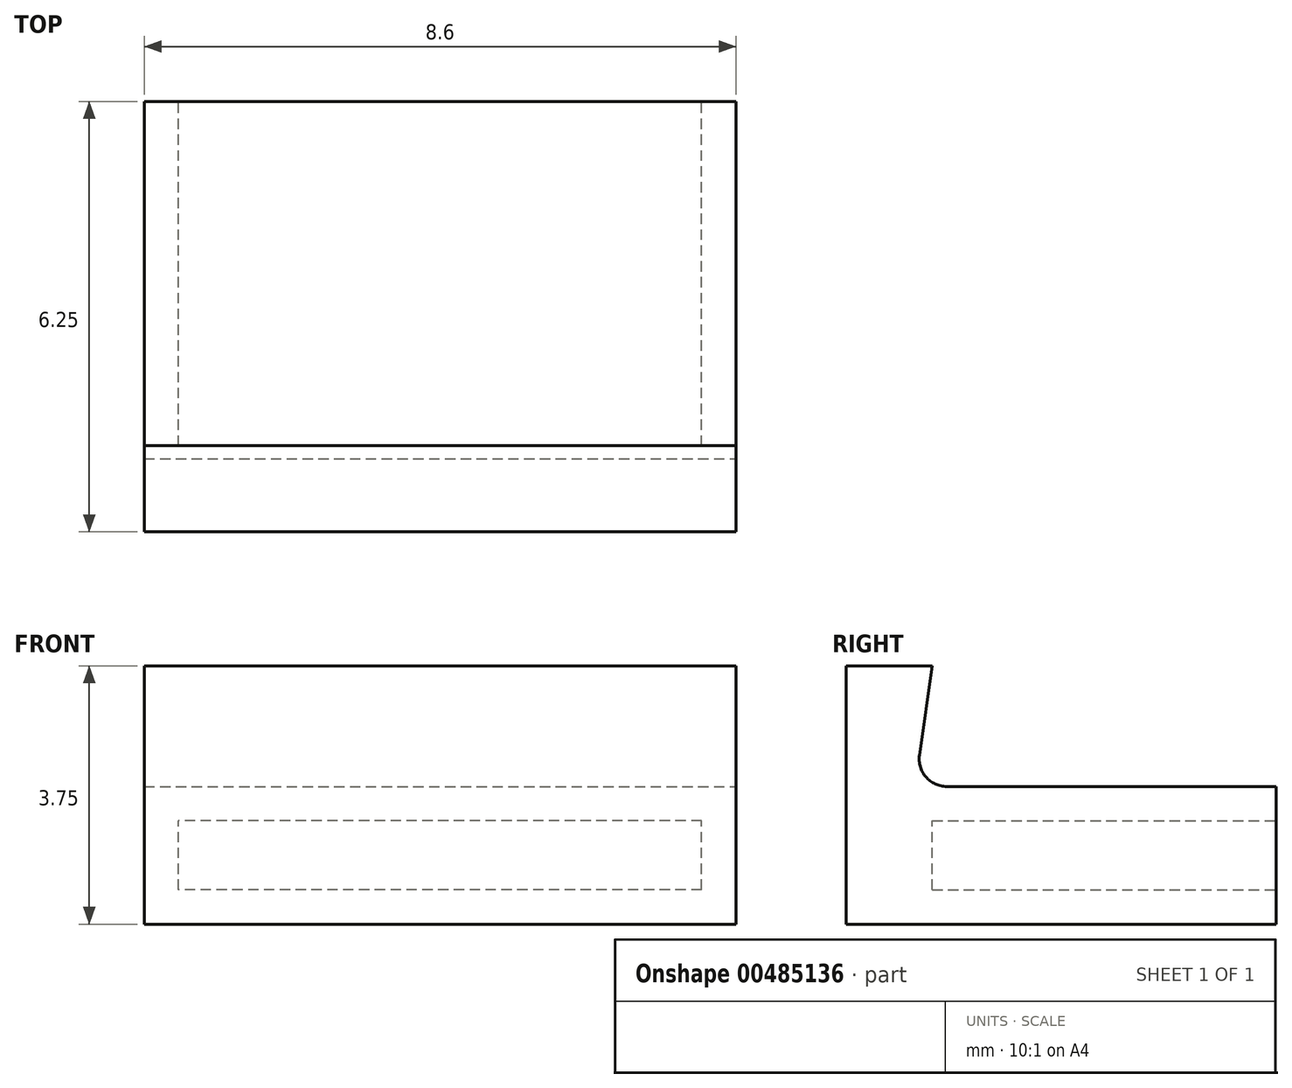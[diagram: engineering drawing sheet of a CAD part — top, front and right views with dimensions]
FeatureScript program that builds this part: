
annotation { "Feature Type Name" : "Feature", "Feature Type Description" : "" }
export const myFeature = defineFeature(function(context is Context, id is Id, definition is map)
    precondition{}
    {
        {
            var Q0;
            Q0=qCreatedBy(makeId("Front.planeOp"),FACE);
            var sketch = newSketch(context, id + "F0", { "sketchPlane" : qUnion([Q0])});
            skLineSegment(sketch, "E0.bottom", {"start": v(3.8, -0.5) * mm, "end": v(-3.8, -0.5) * mm});
            skLineSegment(sketch, "E0.top", {"start": v(3.8, 0.5) * mm, "end": v(-3.8, 0.5) * mm});
            skLineSegment(sketch, "E0.left", {"start": v(3.8, -0.5) * mm, "end": v(3.8, 0.5) * mm});
            skLineSegment(sketch, "E0.right", {"start": v(-3.8, -0.5) * mm, "end": v(-3.8, 0.5) * mm});
            skPoint(sketch, "E0.middle", {"position": v(0, 0) * mm});
            skLineSegment(sketch, "E1.bottom", {"start": v(4.3, -1) * mm, "end": v(-4.3, -1) * mm});
            skLineSegment(sketch, "E1.top", {"start": v(4.3, 1) * mm, "end": v(-4.3, 1) * mm});
            skLineSegment(sketch, "E1.left", {"start": v(4.3, -1) * mm, "end": v(4.3, 1) * mm});
            skLineSegment(sketch, "E1.right", {"start": v(-4.3, -1) * mm, "end": v(-4.3, 1) * mm});
            skSolve(sketch);
        }
        {
            var Q0;
            Q0 = qSketchRegion(id + "F0", true);
            extrude(context, id + "F1", {"entities" : qUnion([Q0]), "depth" : 5 * mm, "offsetDistance" : 25 * mm});
        }
        {
            var Q0;
            Q0=makeQuery(id+"F1.opExtrude","CAP_FACE",FACE,{"disambiguationData":[OSD([sQuery(id+"F0.wireOp",EDGE,"E0.bottom"),sQuery(id+"F0.wireOp",EDGE,"E0.top"),sQuery(id+"F0.wireOp",EDGE,"E0.left"),sQuery(id+"F0.wireOp",EDGE,"E0.right"),sQuery(id+"F0.wireOp",EDGE,"E1.bottom"),sQuery(id+"F0.wireOp",EDGE,"E1.top"),sQuery(id+"F0.wireOp",EDGE,"E1.left"),sQuery(id+"F0.wireOp",EDGE,"E1.right")])],"isStart":false});
            var sketch = newSketch(context, id + "F2", { "sketchPlane" : qUnion([Q0])});
            skLineSegment(sketch, "E2.bottom", {"start": v(-4.3, -1) * mm, "end": v(4.3, -1) * mm});
            skLineSegment(sketch, "E2.top", {"start": v(-4.3, 2.75) * mm, "end": v(4.3, 2.75) * mm});
            skLineSegment(sketch, "E2.left", {"start": v(-4.3, -1) * mm, "end": v(-4.3, 2.75) * mm});
            skLineSegment(sketch, "E2.right", {"start": v(4.3, -1) * mm, "end": v(4.3, 2.75) * mm});
            skSolve(sketch);
        }
        {
            var Q0;
            Q0 = qSketchRegion(id + "F2", true);
            extrude(context, id + "F3", {"entities" : qUnion([Q0]), "operationType" : NewBodyOperationType.ADD, "depth" : 1.25 * mm, "offsetDistance" : 25 * mm});
        }
        {
            var Q0;
            Q0=makeQuery(id+"F3.boolean.opBoolean","MERGE",FACE,{"derivedFrom":[makeQuery(id+"F1.opExtrude","SWEPT_FACE",FACE,{"disambiguationData":[OSD([sQuery(id+"F0.wireOp",EDGE,"E1.left")])]}),makeQuery(id+"F3.opExtrude","SWEPT_FACE",FACE,{"disambiguationData":[OSD([sQuery(id+"F2.wireOp",EDGE,"E2.right")])]})]});
            var sketch = newSketch(context, id + "F4", { "sketchPlane" : qUnion([Q0])});
            skLineSegment(sketch, "E3", {"start": v(-5, 2.75) * mm, "end": v(-5, 1) * mm});
            skLineSegment(sketch, "E4", {"start": v(-5, 1) * mm, "end": v(-5.25, 1) * mm});
            skLineSegment(sketch, "E5", {"start": v(-5.25, 1) * mm, "end": v(-5, 2.75) * mm});
            skSolve(sketch);
        }
        {
            var Q0;
            Q0 = qSketchRegion(id + "F4", true);
            extrude(context, id + "F5", {"entities" : qUnion([Q0]), "operationType" : NewBodyOperationType.REMOVE, "endBound" : BoundingType.THROUGH_ALL, "oppositeDirection" : true, "depth" : 25 * mm, "offsetDistance" : 25 * mm});
        }
        {
            var Q0;
            Q0=makeQuery(id+"F5.boolean.opBoolean","COPY",EDGE,{"derivedFrom":makeQuery(id+"F5.opExtrude","SWEPT_EDGE",EDGE,{"disambiguationData":[OSD([sQuery(id+"F4.wireOp",EDGE,"E4"),sQuery(id+"F4.wireOp",EDGE,"E5")])]})});
            fillet(context, id + "F6", {"entities" : qUnion([Q0]), "radius" : .4 * mm, "tangentPropagation" : true, "allowEdgeOverflow" : false});
        }
    });
